# Revit family: Hager-Univers-IP44-syst-Recessed_mounted-NL-en
name_source: partatom
category: Electrical Equipment
units: mm (PartAtom-declared; Revit-internal decimal feet)

## family parameters
Cut with Voids When Loaded = No
Host = Face
Panel Configuration = Two Columns, Circuits Across
Part Type = Panelboard
Room Calculation Point = No
Round Connector Dimension = Use Diameter
Shared = No

## types (5) — shared parameters
EF000003 - Mounting method = EV001247 - Surface mounted/recessed mounted
EF000007 - Colour = EV000202 - White
EF000049 - Depth = 161 mm  [stored 0.528215 ft]
EF000116 - RAL-number = 9010
EF000118 - With mounting plate = No
EF000218 - Built-in depth = 161 mm  [stored 0.528215 ft]
EF000339 - Type of cover = EV004216 - Door
EF001062 - EMC-version = No
EF001088 - Extension possible = Yes
EF001131 - Internal depth = 160 mm
EF001134 - DIN-rail = Yes
EF001596 - Material housing = EV000179 - Steel
EF002950 - Width in number of modular spacings = 12
EF004462 - Type of closure = EV000154 - Other
EF005474 - Degree of protection (IP) = EV006418 - IP44
EF006244 - Transparent cover/door = No
EF006306 - With lock = No
EF015776 - Earthing terminal block = No
EF015777 - Neutral terminal block = No
EF015941 - Signal passing door = No
HG000002 - With door or cover = Yes
HG000003 - Range = Univers
HG000005 - Thickness = 3 mm  [stored 0.00984252 ft]
HG000006 - Flush mounted = Yes
HG000011 - Empty rows from bottom = No
HG000017 - Distance between poles = 18 mm  [stored 0.0590551 ft]
Manufacturer = Hager
Type Comments = Univers
zero-valued in all types: Default Elevation, HG000007 - Number of empty columns, HG000008 - Number of empty rows

## per-type parameters (varying)
| type | EF000008 - Width | EF000040 - Height | EF000266 - Number of rows | EF000332 - Built-in height | EF000846 - Built-in width | EF009212 - Cover model | HG000001 - Number of columns | HG000004 - Manufacturer reference | HG000009 - Double swing door | HG000010 - Asymmetric doors | Model |
| Recessed mounted IP44 W550 H500 D161 12 Modular spacings - FWB32P | 550 mm | 500 mm  [stored 1.64042 ft] | 6 | 500 mm  [stored 1.64042 ft] | 550 mm | EV000116 - Closed | 2 | FWB32P | No | No | FWB32P |
| Recessed mounted IP44 W550 H650 D161 12 Modular spacings - FWB42P | 550 mm | 650 mm  [stored 2.13255 ft] | 8 | 650 mm  [stored 2.13255 ft] | 550 mm | EV000116 - Closed | 2 | FWB42P | No | No | FWB42P |
| Recessed mounted IP44 W550 H800 D161 12 Modular spacings - FWB52P | 550 mm | 800 mm  [stored 2.62467 ft] | 10 | 800 mm  [stored 2.62467 ft] | 550 mm | EV000116 - Closed | 2 | FWB52P | No | No | FWB52P |
| Recessed mounted IP44 W800 H500 D161 12 Modular spacings - FWB33P | 800 mm  [stored 2.62467 ft] | 500 mm  [stored 1.64042 ft] | 9 | 500 mm  [stored 1.64042 ft] | 800 mm  [stored 2.62467 ft] |  | 3 | FWB33P | Yes | Yes | FWB33P |
| Recessed mounted IP44 W800 H650 D161 12 Modular spacings - FWB43P | 800 mm  [stored 2.62467 ft] | 650 mm  [stored 2.13255 ft] | 12 | 650 mm  [stored 2.13255 ft] | 800 mm  [stored 2.62467 ft] | EV000116 - Closed | 3 | FWB43P | Yes | Yes | FWB43P |

note: [stored X ft] marks values corroborated as IEEE doubles in the binary element streams (Revit-internal decimal feet)

## geometry (parser evidence)
native form markers: Sweep x17
no freeform markers — native parametric forms only
